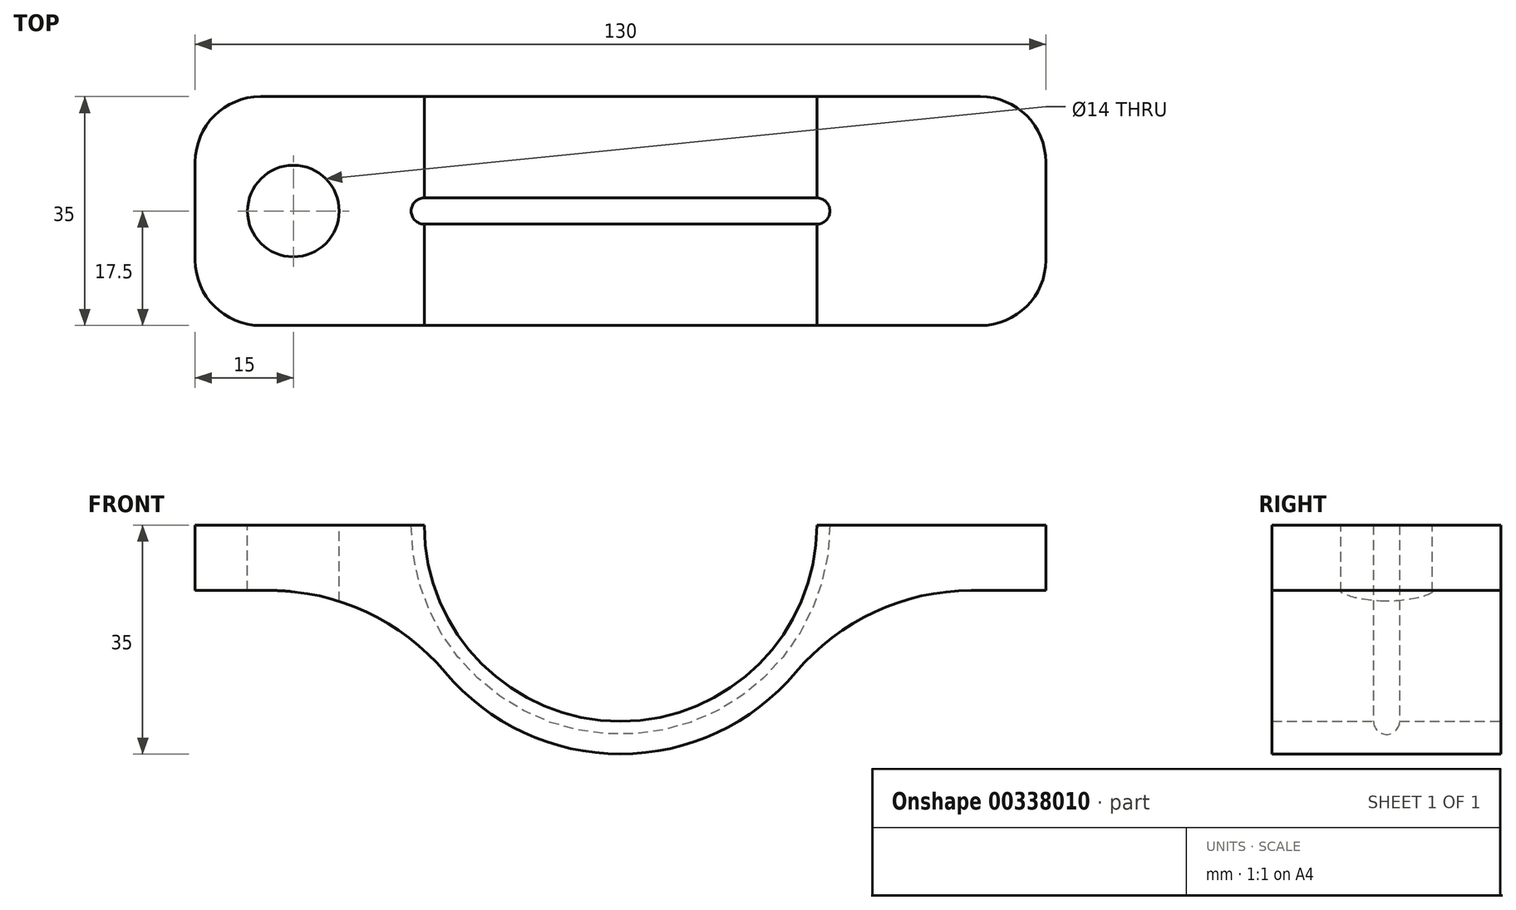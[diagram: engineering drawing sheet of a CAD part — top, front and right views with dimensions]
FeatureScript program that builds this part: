
annotation { "Feature Type Name" : "Feature", "Feature Type Description" : "" }
export const myFeature = defineFeature(function(context is Context, id is Id, definition is map)
    precondition{}
    {
        {
            var Q0;
            Q0=qCreatedBy(makeId("Front.planeOp"),FACE);
            var sketch = newSketch(context, id + "F0", { "sketchPlane" : qUnion([Q0])});
            skArc(sketch, "E0", {"start": v(0, -30) * mm, "mid": v(21.21, -21.21) * mm, "end": v(30, 0) * mm});
            skArc(sketch, "E1", {"start": v(0, -35) * mm, "mid": v(14.8, -31.72) * mm, "end": v(26.8, -22.5) * mm});
            skLineSegment(sketch, "E2", {"start": v(30, 0) * mm, "end": v(65, 0) * mm});
            skLineSegment(sketch, "E3", {"start": v(0, 35) * mm, "end": v(0, -35) * mm, "construction": true});
            skLineSegment(sketch, "E4", {"start": v(65, 0) * mm, "end": v(65, -10) * mm});
            skLineSegment(sketch, "E5", {"start": v(65, -10) * mm, "end": v(53.62, -10) * mm});
            skPoint(sketch, "E6.visualSharp", {"position": v(33.54, -10) * mm});
            skArc(sketch, "E6.filletArc", {"start": v(53.62, -10) * mm, "mid": v(38.83, -13.28) * mm, "end": v(26.8, -22.5) * mm});
            skArc(sketch, "E7.MirrorCS", {"start": v(0, -30) * mm, "mid": v(-21.21, -21.21) * mm, "end": v(-30, 0) * mm});
            skArc(sketch, "E8.MirrorCS", {"start": v(-53.62, -10) * mm, "mid": v(-38.83, -13.28) * mm, "end": v(-26.8, -22.5) * mm});
            skPoint(sketch, "E9.MirrorP", {"position": v(-33.54, -10) * mm});
            skArc(sketch, "E10.MirrorCS", {"start": v(0, -35) * mm, "mid": v(-14.8, -31.72) * mm, "end": v(-26.8, -22.5) * mm});
            skLineSegment(sketch, "E11.MirrorCS", {"start": v(-65, -10) * mm, "end": v(-53.62, -10) * mm});
            skLineSegment(sketch, "E12.MirrorCS", {"start": v(-65, 0) * mm, "end": v(-65, -10) * mm});
            skLineSegment(sketch, "E13.MirrorCS", {"start": v(-30, 0) * mm, "end": v(-65, 0) * mm});
            skSolve(sketch);
        }
        {
            var Q0;
            Q0=makeQuery(id+"F0.imprint","IMPRINT",FACE,{"disambiguationData":[TD([[makeQuery(id+"F0.imprint","IMPRINT",EDGE,{"derivedFrom":sQuery(id+"F0.wireOp",EDGE,"E0")}),-1.0]])]});
            extrude(context, id + "F1", {"entities" : qUnion([Q0]), "depth" : 35 * mm, "symmetric" : true});
        }
        {
            var Q0;
            Q0=makeQuery(id+"F1.opExtrude","SWEPT_FACE",FACE,{"disambiguationData":[OSD([sQuery(id+"F0.wireOp",EDGE,"E13.MirrorCS")])]});
            var sketch = newSketch(context, id + "F2", { "sketchPlane" : qUnion([Q0])});
            skLineSegment(sketch, "E14", {"start": v(0, 33.67) * mm, "end": v(0, -32.76) * mm, "construction": true});
            skCircle(sketch, "E15", {"center": v(-50, 0) * mm, "radius": 7 * mm});
            skCircle(sketch, "E16.MirrorC", {"center": v(50, 0) * mm, "radius": 7 * mm});
            skCircle(sketch, "E17", {"center": v(-30, 0) * mm, "radius": 2 * mm});
            skSolve(sketch);
        }
        {
            var Q0;
            Q0=makeQuery(id+"F2.imprint","IMPRINT",FACE,{"disambiguationData":[TD([[makeQuery(id+"F2.imprint","IMPRINT",EDGE,{"derivedFrom":sQuery(id+"F2.wireOp",EDGE,"E15")}),1.0]])]});
            var Q1;
            Q1=makeQuery(id+"F2.imprint","IMPRINT",FACE,{"disambiguationData":[TD([[makeQuery(id+"F2.imprint","IMPRINT",EDGE,{"derivedFrom":sQuery(id+"F2.wireOp",EDGE,"E16.MirrorC")}),-1.0]])]});
            extrude(context, id + "F3", {"entities" : qUnion([Q0, Q1]), "operationType" : NewBodyOperationType.REMOVE, "oppositeDirection" : true, "depth" : 25 * mm});
        }
        {
            var Q0;
            {var subQ0=sQuery(id+"F2.wireOp",EDGE,"E17");var subQ1=makeQuery(id+"F1.opExtrude","SWEPT_EDGE",EDGE,{"disambiguationData":[OSD([sQuery(id+"F0.wireOp",EDGE,"E7.MirrorCS"),sQuery(id+"F0.wireOp",EDGE,"E13.MirrorCS")])]});var subQ2=makeQuery(id+"F2.imprint","INTERSECT",VERTEX,{"disambiguationData":[OD(0.0)],"derivedFrom":[subQ1,subQ0]});Q0=makeQuery(id+"F2.imprint","IMPRINT",FACE,{"disambiguationData":[TD([[makeQuery(id+"F2.imprint","IMPRINT",EDGE,{"disambiguationData":[TD([[subQ2,-1.0]])],"derivedFrom":subQ0}),1.0]])]});}
            var Q1;
            {var subQ0=sQuery(id+"F2.wireOp",EDGE,"E17");var subQ1=makeQuery(id+"F1.opExtrude","SWEPT_EDGE",EDGE,{"disambiguationData":[OSD([sQuery(id+"F0.wireOp",EDGE,"E7.MirrorCS"),sQuery(id+"F0.wireOp",EDGE,"E13.MirrorCS")])]});var subQ2=makeQuery(id+"F2.imprint","INTERSECT",VERTEX,{"disambiguationData":[OD(0.0)],"derivedFrom":[subQ1,subQ0]});Q1=makeQuery(id+"F2.imprint","IMPRINT",FACE,{"disambiguationData":[TD([[makeQuery(id+"F2.imprint","IMPRINT",EDGE,{"disambiguationData":[TD([[subQ2,1.0]])],"derivedFrom":subQ0}),1.0]])]});}
            var Q2;
            Q2=sQuery(id+"F2.wireOp",EDGE,"E14");
            revolve(context, id + "F4", {"operationType" : NewBodyOperationType.REMOVE, "entities" : qUnion([Q0, Q1]), "axis" : qUnion([Q2]), "revolveType" : RevolveType.FULL, "oppositeDirection" : true});
        }
        {
            var Q0;
            Q0=makeQuery(id+"F1.opExtrude","CAP_EDGE",EDGE,{"disambiguationData":[OSD([sQuery(id+"F0.wireOp",EDGE,"E12.MirrorCS")])],"isStart":true});
            var Q1;
            Q1=makeQuery(id+"F1.opExtrude","CAP_EDGE",EDGE,{"disambiguationData":[OSD([sQuery(id+"F0.wireOp",EDGE,"E12.MirrorCS")])],"isStart":false});
            var Q2;
            Q2=makeQuery(id+"F1.opExtrude","CAP_EDGE",EDGE,{"disambiguationData":[OSD([sQuery(id+"F0.wireOp",EDGE,"E4")])],"isStart":true});
            var Q3;
            Q3=makeQuery(id+"F1.opExtrude","CAP_EDGE",EDGE,{"disambiguationData":[OSD([sQuery(id+"F0.wireOp",EDGE,"E4")])],"isStart":false});
            fillet(context, id + "F5", {"entities" : qUnion([Q0, Q1, Q2, Q3]), "radius" : 10 * mm, "tangentPropagation" : true, "allowEdgeOverflow" : false});
        }
    });
